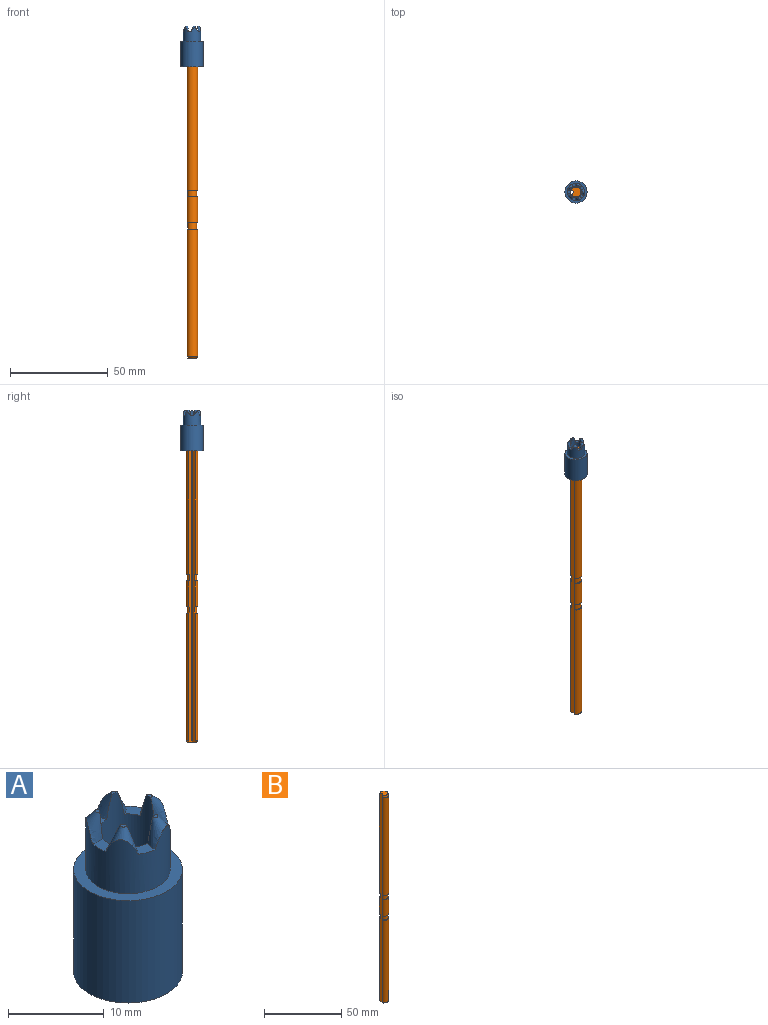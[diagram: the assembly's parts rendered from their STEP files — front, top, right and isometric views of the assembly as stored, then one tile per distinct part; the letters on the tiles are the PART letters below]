
ASSEMBLY  parts=2 mates=1
PART A: 20 faces, bbox 11.7x11.7x21.3 mm
  f0: cone r=1.8mm half-angle=24.8deg, axis (0.34,0,-0.94), area 9.2mm2, adj f1,f2,f3,f4,f16
  f1: plane 0.98x0.75mm, normal (0,0,1), area 0.2mm2, adj f0,f2
  f2: cylinder r=3.04mm len=20.85mm, axis (0,0,-1), area 363.1mm2, adj f0,f1,f4,f5,f6,f7,f8,f9
  f3: cylinder r=4.4mm len=8.8mm, axis (0,0,-1), area 159.2mm2, adj f0,f4,f6,f7,f9,f10,f12,f13
  f4: plane 2.34x2.24mm, normal (0,0,1), area 2.3mm2, adj f0,f2,f3,f6
  f5: plane 0.98x0.84mm, normal (0,0,1), area 0.2mm2, adj f2,f6
  f6: cone r=1.8mm half-angle=24.8deg, axis (0.11,0.33,-0.94), area 9.2mm2, adj f2,f3,f4,f5,f7
  f7: plane 2.22x1.93mm, normal (0,0,1), area 2.3mm2, adj f2,f3,f6,f9
  f8: plane 0.96x0.91mm, normal (0,0,1), area 0.2mm2, adj f2,f9
  f9: cone r=1.8mm half-angle=24.8deg, axis (-0.28,0.2,-0.94), area 9.2mm2, adj f2,f3,f7,f8,f10
  f10: plane 2.02x1.55mm, normal (0,0,1), area 2.3mm2, adj f2,f3,f9,f12
  f11: plane 0.96x0.91mm, normal (0,0,1), area 0.2mm2, adj f2,f12
  f12: cone r=1.8mm half-angle=24.8deg, axis (-0.28,-0.2,-0.94), area 9.2mm2, adj f2,f3,f10,f11,f13
  f13: plane 2.22x1.93mm, normal (0,0,1), area 2.3mm2, adj f2,f3,f12,f14
  f14: cone r=1.8mm half-angle=24.8deg, axis (0.11,-0.33,-0.94), area 9.2mm2, adj f2,f3,f13,f15,f16
  f15: plane 0.98x0.84mm, normal (0,0,1), area 0.2mm2, adj f2,f14
  f16: plane 2.34x2.24mm, normal (0,0,1), area 2.3mm2, adj f0,f2,f3,f14
  f17: cylinder r=5.68mm len=13.05mm, axis (0,0,1), area 465.3mm2, adj f18,f19
  f18: plane 11.35x11.35mm, normal (0,0,-1), area 72.1mm2, adj f2,f17
  f19: plane 11.35x11.35mm, normal (0,0,1), area 40.4mm2, adj f3,f17
PART B: 16 faces, bbox 5.6x5.9x165 mm
  f0: cylinder r=2.95mm len=13.2mm, axis (0,0,-1), area 201.2mm2, adj f2,f4,f11,f15
  f1: cylinder r=2.95mm len=65.4mm, axis (0,0,-1), area 996.7mm2, adj f2,f4,f8,f12
  f2: plane 165.02x1.36mm, normal (-0.71,0.71,0), area 307.8mm2, adj f0,f1,f3,f5,f6,f7,f8,f9
  f3: cylinder r=2.95mm len=77.7mm, axis (0,0,-1), area 1184.2mm2, adj f2,f4,f9,f14
  f4: plane 165.02x1.36mm, normal (-0.71,-0.71,0), area 307.8mm2, adj f0,f1,f3,f5,f6,f7,f8,f9
  f5: cylinder r=0.3mm len=165mm, axis (0,0,-1), area 77.8mm2, adj f2,f4,f6,f7
  f6: plane 5.09x4.75mm, normal (0,0,1), area 18.2mm2, adj f2,f4,f5,f9
  f7: plane 4.69x4.41mm, normal (0,0,-1), area 15.6mm2, adj f2,f4,f5,f8
  f8: cone r=2.95mm half-angle=45deg, axis (0,0,1), area 11.7mm2, adj f1,f2,f4,f7
  f9: cone r=2.54mm half-angle=15deg, axis (0,0,-1), area 22.2mm2, adj f2,f3,f4,f6
  f10: cylinder r=2.4mm len=4.8mm, axis (0,0,-1), area 41.8mm2, adj f2,f4,f11,f12
  f11: plane 5.89x5.45mm, normal (0,0,-1), area 7.6mm2, adj f0,f2,f4,f10
  f12: plane 5.89x5.45mm, normal (0,0,1), area 7.6mm2, adj f1,f2,f4,f10
  f13: cylinder r=2.4mm len=4.8mm, axis (0,0,-1), area 41.8mm2, adj f2,f4,f14,f15
  f14: plane 5.89x5.45mm, normal (0,0,-1), area 7.6mm2, adj f2,f3,f4,f13
  f15: plane 5.89x5.45mm, normal (0,0,1), area 7.6mm2, adj f0,f2,f4,f13
PLACE A at identity fixed
PLACE B t=(0,0,-162.15)mm
MATE fastened B.f0 <-> A.f2  axis (0,0,1) through (0,0,2.85)mm
